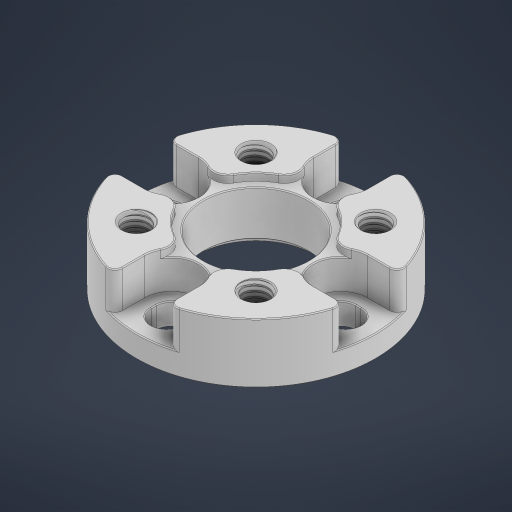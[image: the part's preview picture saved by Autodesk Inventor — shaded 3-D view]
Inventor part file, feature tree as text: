
AUTODESK INVENTOR PART (.ipt)
format: ipt  version: 2023 (Build 270158000, 158)  size: 1,540,608 bytes
history: native  units: in
note: dims shown in document units (in); Inventor stores cm internally (conversion verified against a paired STEP export)
features: chamfer x1
ambient origin geometry x8: Origin, YZ Plane, XZ Plane, XY Plane, X Axis, Y Axis, Z Axis, Center Point
bodies: Solid1 (feature_tree)
feature tree (1):
  chamfer  "Chamfer2"  [1 undecoded]
note: 1 required parameter value undecoded (feature->parameter linkage not recoverable at this tier; creation-order binding heuristic only, values carry confidence <= 0.55)
